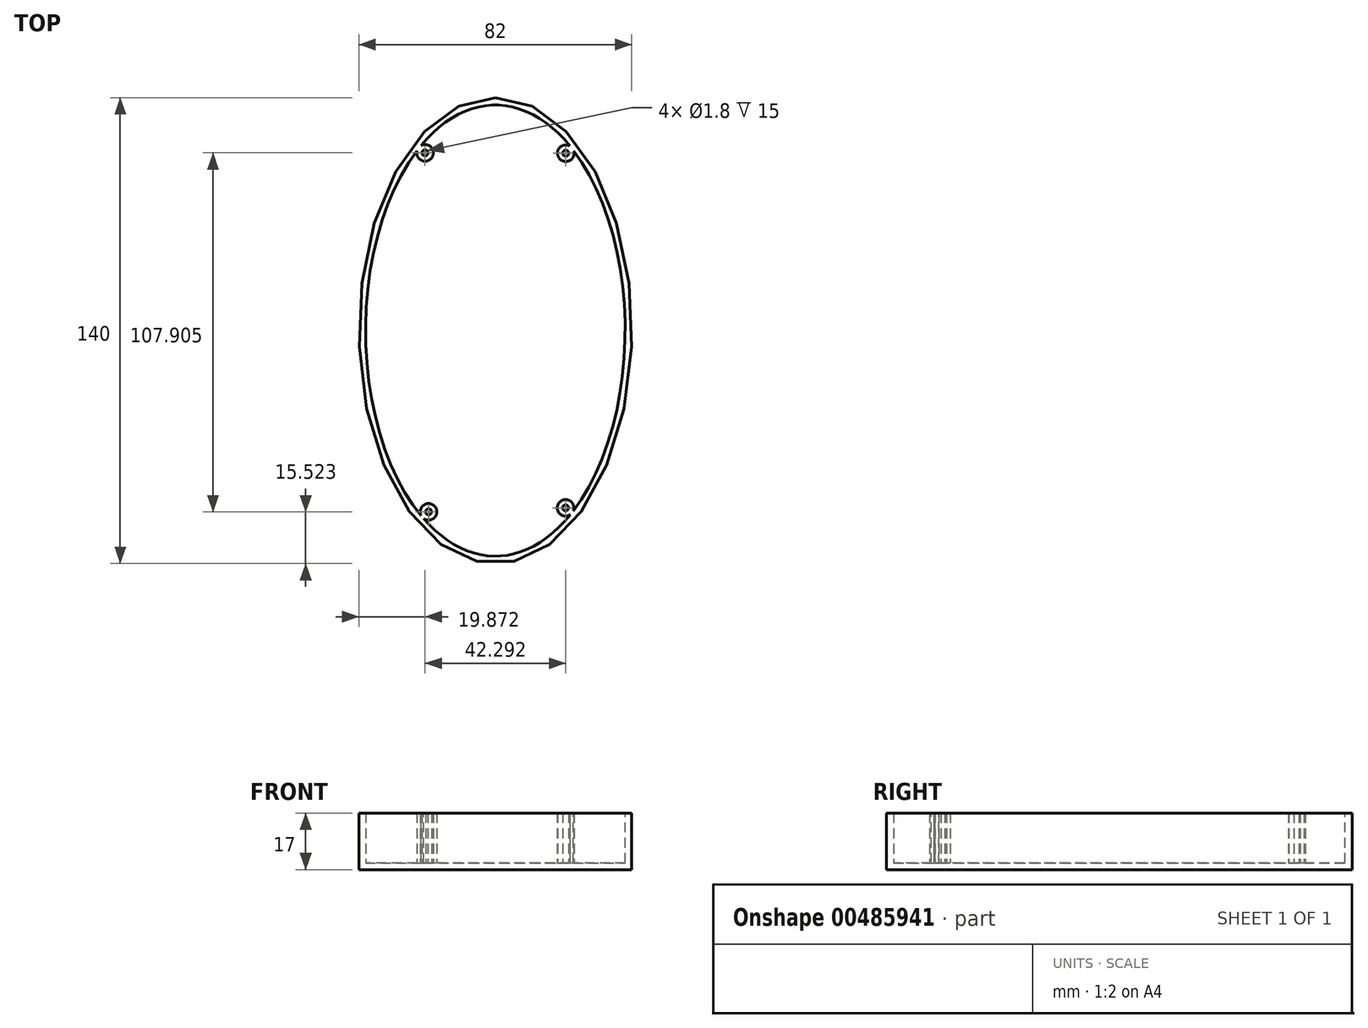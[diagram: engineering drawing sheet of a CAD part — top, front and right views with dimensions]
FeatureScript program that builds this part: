
annotation { "Feature Type Name" : "Feature", "Feature Type Description" : "" }
export const myFeature = defineFeature(function(context is Context, id is Id, definition is map)
    precondition{}
    {
        {
            var Q0;
            Q0=qCreatedBy(makeId("Top.planeOp"),FACE);
            var sketch = newSketch(context, id + "F0", { "sketchPlane" : qUnion([Q0])});
            skEllipse(sketch, "E0", {"center": v(-6.22, 3.26) * mm, "majorRadius": 70 * mm, "minorRadius": 41 * mm, "majorAxis": v(0, 1)});
            skSolve(sketch);
        }
        {
            var Q0;
            Q0=qSketchRegion(id+"F0",true);
            extrude(context, id + "F1", {"entities" : qUnion([Q0]), "depth" : 17 * mm, "offsetDistance" : 25 * mm});
        }
        {
            var Q0;
            Q0=makeQuery(id+"F1.opExtrude","CAP_FACE",FACE,{"disambiguationData":[OSD([sQuery(id+"F0.wireOp",EDGE,"E0")])],"isStart":false});
            var sketch = newSketch(context, id + "F2", { "sketchPlane" : qUnion([Q0])});
            skEllipse(sketch, "E1", {"center": v(-6.22, 3.26) * mm, "majorRadius": 67.8 * mm, "minorRadius": 39 * mm, "majorAxis": v(0, 1)});
            skSolve(sketch);
        }
        {
            var Q0;
            Q0=makeQuery(id+"F2.imprint","IMPRINT",FACE,{"disambiguationData":[TD([[makeQuery(id+"F2.imprint","IMPRINT",EDGE,{"derivedFrom":sQuery(id+"F2.wireOp",EDGE,"E1")}),1.0]])]});
            extrude(context, id + "F3", {"entities" : qUnion([Q0]), "operationType" : NewBodyOperationType.REMOVE, "oppositeDirection" : true, "depth" : 15 * mm});
        }
        {
            var Q0;
            Q0=makeQuery(id+"F3.boolean.opBoolean","COPY",FACE,{"derivedFrom":makeQuery(id+"F3.opExtrude","CAP_FACE",FACE,{"disambiguationData":[OSD([sQuery(id+"F2.wireOp",EDGE,"E1")])],"isStart":false})});
            var sketch = newSketch(context, id + "F4", { "sketchPlane" : qUnion([Q0])});
            skCircle(sketch, "E2", {"center": v(-27.35, 56.69) * mm, "radius": 2.5 * mm});
            skPoint(sketch, "E2.first.point", {"position": v(-28.49, 58.91) * mm});
            skPoint(sketch, "E2.second.point", {"position": v(-26.1, 54.53) * mm});
            skPoint(sketch, "E2.third.point", {"position": v(-27.44, 54.19) * mm});
            skCircle(sketch, "E3", {"center": v(-27.35, 56.69) * mm, "radius": 0.9 * mm});
            skSolve(sketch);
        }
        {
            var Q0;
            {var subQ0=sQuery(id+"F4.wireOp",EDGE,"E2");var subQ1=makeQuery(id+"F3.boolean.opBoolean","COPY",EDGE,{"derivedFrom":makeQuery(id+"F3.opExtrude","CAP_EDGE",EDGE,{"disambiguationData":[OSD([sQuery(id+"F2.wireOp",EDGE,"E1")])],"isStart":false})});var subQ2=makeQuery(id+"F4.imprint","INTERSECT",VERTEX,{"disambiguationData":[OD(0.0)],"derivedFrom":[subQ1,subQ0]});Q0=makeQuery(id+"F4.imprint","IMPRINT",FACE,{"disambiguationData":[TD([[makeQuery(id+"F4.imprint","IMPRINT",EDGE,{"disambiguationData":[TD([[subQ2,-1.0]])],"derivedFrom":subQ0}),1.0]])]});}
            extrude(context, id + "F5", {"entities" : qUnion([Q0]), "operationType" : NewBodyOperationType.ADD, "depth" : 15 * mm});
        }
        {
            var Q0;
            Q0=makeQuery(id+"F3.boolean.opBoolean","COPY",FACE,{"derivedFrom":makeQuery(id+"F3.opExtrude","CAP_FACE",FACE,{"disambiguationData":[OSD([sQuery(id+"F2.wireOp",EDGE,"E1")])],"isStart":false})});
            var sketch = newSketch(context, id + "F6", { "sketchPlane" : qUnion([Q0])});
            skCircle(sketch, "E4", {"center": v(14.94, 56.58) * mm, "radius": 2.5 * mm});
            skPoint(sketch, "E4.first.point", {"position": v(12.51, 56) * mm});
            skPoint(sketch, "E4.second.point", {"position": v(17.34, 57.29) * mm});
            skPoint(sketch, "E4.third.point", {"position": v(16.01, 54.32) * mm});
            skCircle(sketch, "E5", {"center": v(14.94, 56.58) * mm, "radius": 0.9 * mm});
            skSolve(sketch);
        }
        {
            var Q0;
            {var subQ0=sQuery(id+"F6.wireOp",EDGE,"E4");var subQ1=makeQuery(id+"F3.boolean.opBoolean","COPY",EDGE,{"derivedFrom":makeQuery(id+"F3.opExtrude","CAP_EDGE",EDGE,{"disambiguationData":[OSD([sQuery(id+"F2.wireOp",EDGE,"E1")])],"isStart":false})});var subQ2=makeQuery(id+"F6.imprint","INTERSECT",VERTEX,{"disambiguationData":[OD(0.0)],"derivedFrom":[subQ1,subQ0]});Q0=makeQuery(id+"F6.imprint","IMPRINT",FACE,{"disambiguationData":[TD([[makeQuery(id+"F6.imprint","IMPRINT",EDGE,{"disambiguationData":[TD([[subQ2,1.0]])],"derivedFrom":subQ0}),1.0]])]});}
            extrude(context, id + "F7", {"entities" : qUnion([Q0]), "operationType" : NewBodyOperationType.ADD, "depth" : 15 * mm});
        }
        {
            var Q0;
            Q0=makeQuery(id+"F3.boolean.opBoolean","COPY",FACE,{"derivedFrom":makeQuery(id+"F3.opExtrude","CAP_FACE",FACE,{"disambiguationData":[OSD([sQuery(id+"F2.wireOp",EDGE,"E1")])],"isStart":false})});
            var sketch = newSketch(context, id + "F8", { "sketchPlane" : qUnion([Q0])});
            skCircle(sketch, "E6", {"center": v(-26.28, -51.22) * mm, "radius": 2.5 * mm});
            skPoint(sketch, "E6.first.point", {"position": v(-28.49, -50.03) * mm});
            skPoint(sketch, "E6.second.point", {"position": v(-24.98, -49.08) * mm});
            skPoint(sketch, "E6.third.point", {"position": v(-28.49, -52.4) * mm});
            skCircle(sketch, "E7", {"center": v(-26.28, -51.22) * mm, "radius": 0.9 * mm});
            skSolve(sketch);
        }
        {
            var Q0;
            {var subQ0=sQuery(id+"F8.wireOp",EDGE,"E6");var subQ1=makeQuery(id+"F7.boolean.opBoolean","SPLIT",EDGE,{"disambiguationData":[OD(0.0)],"derivedFrom":makeQuery(id+"F3.boolean.opBoolean","COPY",EDGE,{"derivedFrom":makeQuery(id+"F3.opExtrude","CAP_EDGE",EDGE,{"disambiguationData":[OSD([sQuery(id+"F2.wireOp",EDGE,"E1")])],"isStart":false})})});var subQ2=makeQuery(id+"F8.imprint","INTERSECT",VERTEX,{"disambiguationData":[OD(0.0)],"derivedFrom":[subQ1,subQ0]});Q0=makeQuery(id+"F8.imprint","IMPRINT",FACE,{"disambiguationData":[TD([[makeQuery(id+"F8.imprint","IMPRINT",EDGE,{"disambiguationData":[TD([[subQ2,1.0]])],"derivedFrom":subQ0}),1.0]])]});}
            extrude(context, id + "F9", {"entities" : qUnion([Q0]), "operationType" : NewBodyOperationType.ADD, "depth" : 15 * mm});
        }
        {
            var Q0;
            Q0=makeQuery(id+"F3.boolean.opBoolean","COPY",FACE,{"derivedFrom":makeQuery(id+"F3.opExtrude","CAP_FACE",FACE,{"disambiguationData":[OSD([sQuery(id+"F2.wireOp",EDGE,"E1")])],"isStart":false})});
            var sketch = newSketch(context, id + "F10", { "sketchPlane" : qUnion([Q0])});
            skCircle(sketch, "E8", {"center": v(14.89, -50.02) * mm, "radius": 2.5 * mm});
            skPoint(sketch, "E8.first.point", {"position": v(17.2, -50.95) * mm});
            skPoint(sketch, "E8.second.point", {"position": v(12.45, -49.45) * mm});
            skPoint(sketch, "E8.third.point", {"position": v(13.95, -47.7) * mm});
            skCircle(sketch, "E9", {"center": v(14.89, -50.02) * mm, "radius": 0.9 * mm});
            skSolve(sketch);
        }
        {
            var Q0;
            {var subQ0=sQuery(id+"F10.wireOp",EDGE,"E8");var subQ1=sQuery(id+"F2.wireOp",EDGE,"E1");var subQ2=makeQuery(id+"F9.boolean.opBoolean","SPLIT",EDGE,{"disambiguationData":[TD([makeQuery(id+"F7.opExtrude","SWEPT_FACE",FACE,{"disambiguationData":[OSD([sQuery(id+"F6.wireOp",EDGE,"E4")])]})])],"derivedFrom":makeQuery(id+"F7.boolean.opBoolean","SPLIT",EDGE,{"disambiguationData":[OD(0.0)],"derivedFrom":makeQuery(id+"F3.boolean.opBoolean","COPY",EDGE,{"derivedFrom":makeQuery(id+"F3.opExtrude","CAP_EDGE",EDGE,{"disambiguationData":[OSD([subQ1])],"isStart":false})})})});var subQ3=makeQuery(id+"F10.imprint","INTERSECT",VERTEX,{"disambiguationData":[OD(0.0)],"derivedFrom":[subQ2,subQ0]});Q0=makeQuery(id+"F10.imprint","IMPRINT",FACE,{"disambiguationData":[TD([[makeQuery(id+"F10.imprint","IMPRINT",EDGE,{"disambiguationData":[TD([[subQ3,-1.0]])],"derivedFrom":subQ0}),1.0]])]});}
            extrude(context, id + "F11", {"entities" : qUnion([Q0]), "operationType" : NewBodyOperationType.ADD, "depth" : 15 * mm});
        }
        {
            var Q0;
            {var subQ0=sQuery(id+"F2.wireOp",EDGE,"E1");Q0=makeQuery(id+"F11.boolean.opBoolean","MERGE",FACE,{"derivedFrom":[makeQuery(id+"F9.boolean.opBoolean","MERGE",FACE,{"derivedFrom":[makeQuery(id+"F7.boolean.opBoolean","MERGE",FACE,{"derivedFrom":[makeQuery(id+"F5.boolean.opBoolean","MERGE",FACE,{"derivedFrom":[makeQuery(id+"F1.opExtrude","CAP_FACE",FACE,{"disambiguationData":[OSD([sQuery(id+"F0.wireOp",EDGE,"E0")])],"isStart":false}),makeQuery(id+"F5.opExtrude","CAP_FACE",FACE,{"disambiguationData":[OSD([subQ0,sQuery(id+"F4.wireOp",EDGE,"E2")])],"isStart":false})]}),makeQuery(id+"F7.opExtrude","CAP_FACE",FACE,{"disambiguationData":[OSD([subQ0,sQuery(id+"F6.wireOp",EDGE,"E4")])],"isStart":false})]}),makeQuery(id+"F9.opExtrude","CAP_FACE",FACE,{"disambiguationData":[OSD([subQ0,sQuery(id+"F8.wireOp",EDGE,"E6")])],"isStart":false})]}),makeQuery(id+"F11.opExtrude","CAP_FACE",FACE,{"disambiguationData":[OSD([subQ0,sQuery(id+"F10.wireOp",EDGE,"E8")])],"isStart":false})]});}
            var sketch = newSketch(context, id + "F12", { "sketchPlane" : qUnion([Q0])});
            skSolve(sketch);
        }
        {
            var Q0;
            {var subQ8=sQuery(id+"F0.wireOp",EDGE,"E0");Q0=makeQuery(id+"F12.imprint","IMPRINT",FACE,{"disambiguationData":[TD([[makeQuery(id+"F12.imprint","IMPRINT",EDGE,{"derivedFrom":makeQuery(id+"F1.opExtrude","CAP_EDGE",EDGE,{"disambiguationData":[OSD([subQ8])],"isStart":false})}),1.0]])]});}
            var sketch = newSketch(context, id + "F13", { "sketchPlane" : qUnion([Q0])});
            skCircle(sketch, "E10.0", {"center": v(-27.35, 56.69) * mm, "radius": 0.9 * mm});
            skCircle(sketch, "E11.0", {"center": v(14.94, 56.58) * mm, "radius": 0.9 * mm});
            skCircle(sketch, "E12.0", {"center": v(-26.28, -51.22) * mm, "radius": 0.9 * mm});
            skCircle(sketch, "E13.0", {"center": v(14.89, -50.02) * mm, "radius": 0.9 * mm});
            skSolve(sketch);
        }
        {
            var Q0;
            Q0=qSketchRegion(id+"F13",true);
            extrude(context, id + "F14", {"entities" : qUnion([Q0]), "operationType" : NewBodyOperationType.REMOVE, "oppositeDirection" : true, "depth" : 9 * mm, "offsetDistance" : 25 * mm});
        }
    });
